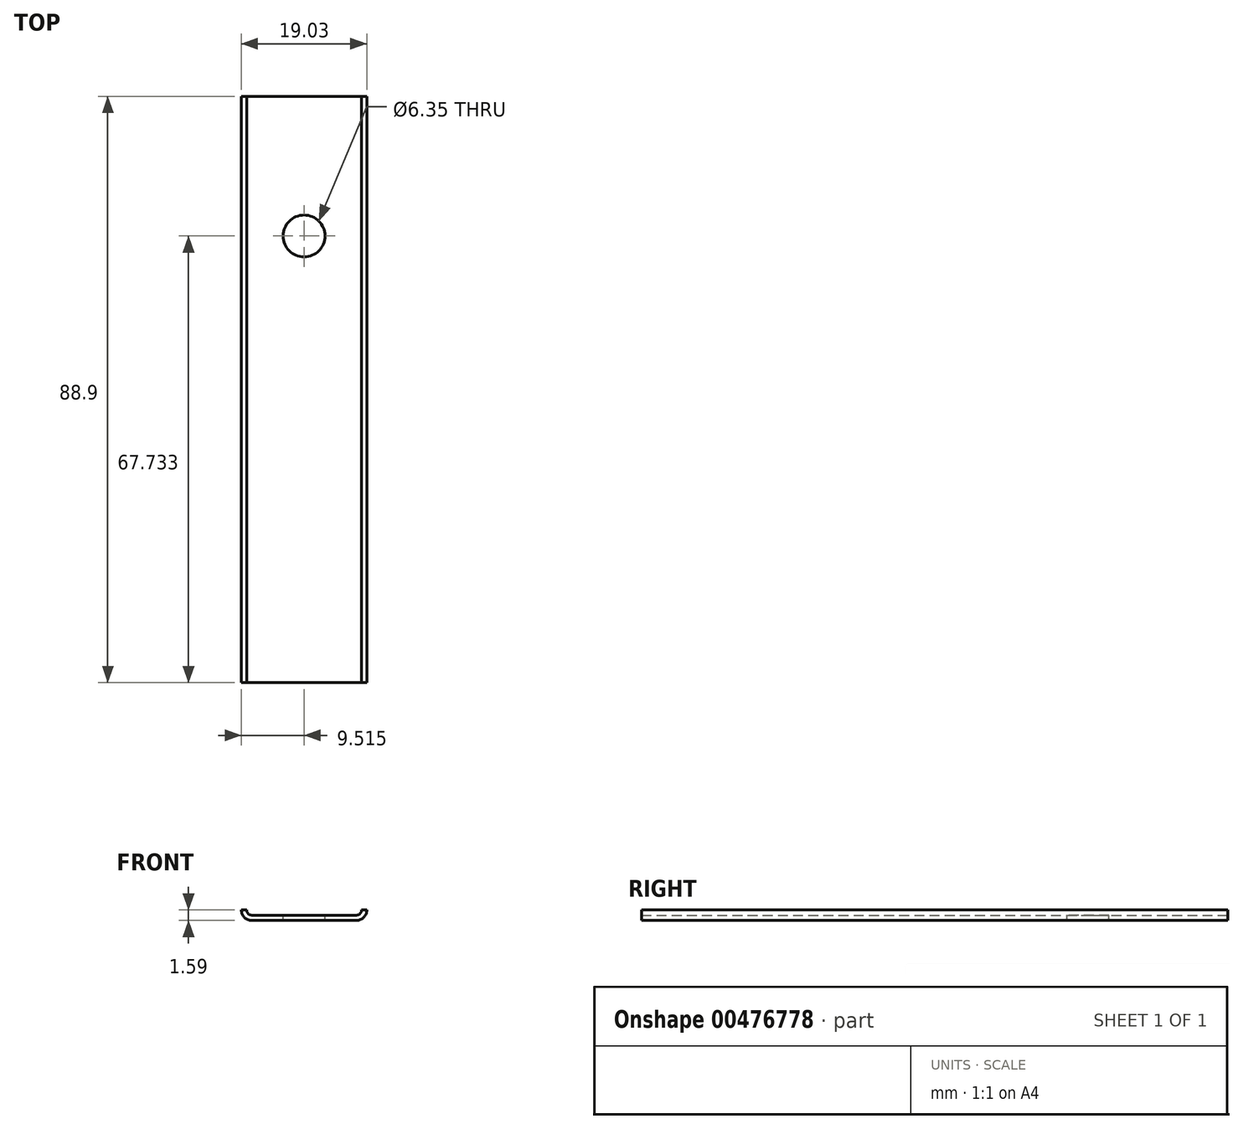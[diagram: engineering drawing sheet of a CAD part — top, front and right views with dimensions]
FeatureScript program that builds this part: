
annotation { "Feature Type Name" : "Feature", "Feature Type Description" : "" }
export const myFeature = defineFeature(function(context is Context, id is Id, definition is map)
    precondition{}
    {
        {
            var Q0;
            Q0=qCreatedBy(makeId("Front.planeOp"),FACE);
            var sketch = newSketch(context, id + "F0", { "sketchPlane" : qUnion([Q0])});
            skLineSegment(sketch, "E0", {"start": v(0, 0) * mm, "end": v(15.85, 0) * mm});
            skLineSegment(sketch, "E1", {"start": v(0, 0.8) * mm, "end": v(0, 1.59) * mm});
            skArc(sketch, "E2", {"start": v(-1.59, 1.59) * mm, "mid": v(-1.12, 0.46) * mm, "end": v(0, 0) * mm});
            skLineSegment(sketch, "E3.0", {"start": v(0, 0.8) * mm, "end": v(15.85, 0.8) * mm});
            skArc(sketch, "E4", {"start": v(-0.79, 1.59) * mm, "mid": v(-0.56, 1.03) * mm, "end": v(0, 0.8) * mm});
            skLineSegment(sketch, "E5", {"start": v(-0.79, 1.59) * mm, "end": v(-1.59, 1.59) * mm});
            skLineSegment(sketch, "E6", {"start": v(7.92, 0.8) * mm, "end": v(7.92, 1.35) * mm});
            skLineSegment(sketch, "E7.MirrorCS", {"start": v(16.64, 1.59) * mm, "end": v(17.44, 1.59) * mm});
            skArc(sketch, "E8.MirrorCS", {"start": v(16.64, 1.59) * mm, "mid": v(16.4, 1.03) * mm, "end": v(15.85, 0.8) * mm});
            skArc(sketch, "E9.MirrorCS", {"start": v(17.44, 1.59) * mm, "mid": v(16.97, 0.46) * mm, "end": v(15.85, 0) * mm});
            skPoint(sketch, "E10.orphan", {"position": v(1.38, 0.8) * mm});
            skPoint(sketch, "E11.orphan", {"position": v(14.47, 0.8) * mm});
            skSolve(sketch);
        }
        {
            var Q0;
            Q0=makeQuery(id+"F0.imprint","IMPRINT",FACE,{"disambiguationData":[TD([[makeQuery(id+"F0.imprint","IMPRINT",EDGE,{"derivedFrom":sQuery(id+"F0.wireOp",EDGE,"E0")}),1.0]])]});
            extrude(context, id + "F1", {"entities" : qUnion([Q0]), "depth" : 101.6 * mm, "hasSecondDirection" : true, "secondDirectionOppositeDirection" : false, "secondDirectionDepth" : 12.7 * mm});
        }
        {
            var Q0;
            Q0=makeQuery(id+"F1.opExtrude","SWEPT_FACE",FACE,{"disambiguationData":[OSD([sQuery(id+"F0.wireOp",EDGE,"E3.0")])]});
            var sketch = newSketch(context, id + "F2", { "sketchPlane" : qUnion([Q0])});
            skLineSegment(sketch, "E12", {"start": v(15.85, -101.6) * mm, "end": v(15.85, -12.7) * mm});
            skLineSegment(sketch, "E13", {"start": v(0, -12.7) * mm, "end": v(0, -33.87) * mm});
            skLineSegment(sketch, "E14", {"start": v(0, -33.87) * mm, "end": v(15.85, -33.87) * mm});
            skLineSegment(sketch, "E15", {"start": v(0, -12.7) * mm, "end": v(7.92, -33.87) * mm});
            skCircle(sketch, "E16", {"center": v(7.92, -33.87) * mm, "radius": 3.18 * mm});
            skSolve(sketch);
        }
        {
            var Q0;
            {var subQ0=sQuery(id+"F2.wireOp",EDGE,"FPQ5Zdq6-sfdL-oR25-akEA-jttTdm4hjQQ7");var subQ1=sQuery(id+"F2.wireOp",EDGE,"aHWidaNG-uPmg-M7WA-tI41-5Ri5BRZmuhVB");var subQ2=makeQuery(id+"F2.imprint","INTERSECT",VERTEX,{"disambiguationData":[OD(0.0)],"derivedFrom":[subQ1,subQ0]});Q0=makeQuery(id+"F2.imprint","IMPRINT",FACE,{"disambiguationData":[TD([[makeQuery(id+"F2.imprint","IMPRINT",EDGE,{"disambiguationData":[TD([[subQ2,-1.0]])],"derivedFrom":subQ1}),1.0]])]});}
            var Q1;
            {var subQ0=sQuery(id+"F2.wireOp",EDGE,"hxGqY3D6-AGkg-9vP5-LXb4-GV6bEmG9bxUK");var subQ1=sQuery(id+"F2.wireOp",EDGE,"aHWidaNG-uPmg-M7WA-tI41-5Ri5BRZmuhVB");var subQ2=makeQuery(id+"F2.imprint","INTERSECT",VERTEX,{"derivedFrom":[subQ1,subQ0]});Q1=makeQuery(id+"F2.imprint","IMPRINT",FACE,{"disambiguationData":[TD([[makeQuery(id+"F2.imprint","IMPRINT",EDGE,{"disambiguationData":[TD([[subQ2,-1.0]])],"derivedFrom":subQ1}),1.0]])]});}
            var Q2;
            {var subQ0=sQuery(id+"F2.wireOp",EDGE,"hxGqY3D6-AGkg-9vP5-LXb4-GV6bEmG9bxUK");var subQ1=sQuery(id+"F2.wireOp",EDGE,"aHWidaNG-uPmg-M7WA-tI41-5Ri5BRZmuhVB");var subQ2=makeQuery(id+"F2.imprint","INTERSECT",VERTEX,{"derivedFrom":[subQ1,subQ0]});Q2=makeQuery(id+"F2.imprint","IMPRINT",FACE,{"disambiguationData":[TD([[makeQuery(id+"F2.imprint","IMPRINT",EDGE,{"disambiguationData":[TD([[subQ2,-1.0]])],"derivedFrom":subQ1}),-1.0]])]});}
            var Q3;
            {var subQ0=sQuery(id+"F2.wireOp",EDGE,"FPQ5Zdq6-sfdL-oR25-akEA-jttTdm4hjQQ7");var subQ1=sQuery(id+"F2.wireOp",EDGE,"aHWidaNG-uPmg-M7WA-tI41-5Ri5BRZmuhVB");var subQ2=makeQuery(id+"F2.imprint","INTERSECT",VERTEX,{"disambiguationData":[OD(0.0)],"derivedFrom":[subQ1,subQ0]});Q3=makeQuery(id+"F2.imprint","IMPRINT",FACE,{"disambiguationData":[TD([[makeQuery(id+"F2.imprint","IMPRINT",EDGE,{"disambiguationData":[TD([[subQ2,-1.0]])],"derivedFrom":subQ1}),-1.0]])]});}
            var Q4;
            {var subQ0=sQuery(id+"F2.wireOp",EDGE,"E15");var subQ1=sQuery(id+"F2.wireOp",EDGE,"E14");var subQ2=makeQuery(id+"F2.imprint","INTERSECT",VERTEX,{"derivedFrom":[subQ1,subQ0]});Q4=makeQuery(id+"F2.imprint","IMPRINT",FACE,{"disambiguationData":[TD([[makeQuery(id+"F2.imprint","IMPRINT",EDGE,{"disambiguationData":[TD([[subQ2,1.0]])],"derivedFrom":subQ1}),1.0]])]});}
            var Q5;
            {var subQ0=sQuery(id+"F2.wireOp",EDGE,"E15");var subQ1=sQuery(id+"F2.wireOp",EDGE,"E14");var subQ2=makeQuery(id+"F2.imprint","INTERSECT",VERTEX,{"derivedFrom":[subQ1,subQ0]});Q5=makeQuery(id+"F2.imprint","IMPRINT",FACE,{"disambiguationData":[TD([[makeQuery(id+"F2.imprint","IMPRINT",EDGE,{"disambiguationData":[TD([[subQ2,-1.0]])],"derivedFrom":subQ1}),1.0]])]});}
            var Q6;
            {var subQ0=sQuery(id+"F2.wireOp",EDGE,"E14");var subQ1=makeQuery(id+"F2.imprint","INTERSECT",VERTEX,{"derivedFrom":[subQ0,sQuery(id+"F2.wireOp",EDGE,"E15")]});Q6=makeQuery(id+"F2.imprint","IMPRINT",FACE,{"disambiguationData":[TD([[makeQuery(id+"F2.imprint","IMPRINT",EDGE,{"disambiguationData":[TD([[subQ1,1.0]])],"derivedFrom":subQ0}),-1.0]])]});}
            var Q7;
            Q7=makeQuery(id+"F1.opExtrude","SWEPT_FACE",FACE,{"disambiguationData":[OSD([sQuery(id+"F0.wireOp",EDGE,"E0")])]});
            extrude(context, id + "F3", {"entities" : qUnion([Q0, Q1, Q2, Q3, Q4, Q5, Q6]), "operationType" : NewBodyOperationType.REMOVE, "endBound" : BoundingType.UP_TO_SURFACE, "oppositeDirection" : true, "endBoundEntityFace" : qUnion([Q7]), "depth" : 25.4 * mm});
        }
    });
